# Revit family: QF_Franke_CW230_en
name_source: partatom
category: Specialty Equipment
revit_build: Autodesk Revit 2018 (Build: 20170223_1515(x64)
units: mm (PartAtom-declared; Revit-internal decimal feet)

## family parameters
Always vertical = Yes
Cut with Voids When Loaded = No
OmniClass Number = 23.40.40.00
OmniClass Title = Food Service Equipment and Furnishings
Part Type = Normal
Room Calculation Point = No
Round Connector Dimension = Use Diameter
Shared = No
Work Plane-Based = No

## types (1)
- 220-240V 1L N PE 0,45 À 120 W 10 À 50-60Hz - (CH/EU)
    Assembly Code = E1090320
    CE Approved = Yes
    Conn Conduit = Yes
    Cover front = <By Category>
    Cycle = 50 Hz
    Cycle Alternative = 60 Hz
    Depth Actual = 420 mm  [stored 1.37795 ft]
    ETL Approved = No
    Energy efficiency label = -
    Energy loss acc. to DIN 18873 = 0
    Height Actual = 455 mm
    Hygiene Approval = -
    Installed By = Franke technician or authorized Franke partner company
    Keynote = 11 46 23
    Length Actual = 330 mm
    Main switch integrated = Yes
    Manufacturer = Animo B.V.
    Max Overcurrent Protection = 10 A
    Model = CW230
    Noise emission = < 70 dB (A)
    Number of Nutral Conductors = 1
    Number of Poles = 1
    Number of Protective Conductors = 1
    Omniclass Number = 23.40.40.14.14.14
    Power consumption = 0 A
    Specification by Manufacturer = The cup warmer CW230 is designed for storage and preheating of cups and glasses for the preparation of coffee specialties..
    Storage coffee cups app. = 60
    Storage espresso cups app. = 140
    URL = https://www.franke.com
    URL Critical Spares List = https://shop.franke.com
    URL Cutsheet = https://www.franke.com
    URL Manufacturer = https://www.franke.com
    Volts max. = 240 V
    Volts min. = 220 V
    Warranty Duration = 12 Mon.
    Watts max. = 0 W
    Watts min. = 120 W
    Weight = 11.00 kg

note: [stored X ft] marks values corroborated as IEEE doubles in the binary element streams (Revit-internal decimal feet)
